# Revit family: Base_Cabinets-Teknion-RHBW_Base_Cabinet_with_Drawers-R2018
name_source: partatom
category: Furniture
revit_build: Autodesk Revit 2018 (Build: 20190510_1515(x64)
units: mm (PartAtom-declared; Revit-internal decimal feet)

## family parameters
Always vertical = Yes
Cut with Voids When Loaded = No
OmniClass Number = 23.40.20.00
OmniClass Title = General Furniture and Specialties
Room Calculation Point = No
Shared = Yes
Work Plane-Based = No

## types (8) — shared parameters
Assembly Code = E2020200
Manufacturer = Teknion
Manufacturer Fax = 416.661.4586
Part Number = RHBW
Product Documentation Link = https://www.teknion.com
Product Line = Modular Cabinets
Product Page URL = https://www.teknion.com
Series = Modular Cabinets
Sustainability Data = https://www.teknion.com
URL = www.teknion.com
Unit Weight URL = http://www.teknion.com
Warranty = http://www.teknion.com

## per-type parameters (varying)
| type | Depth | Description | Four Drawers | Height | Model | Three Drawers | Three Drawers Hole Depth |
| Three Drawers, 24" Depth, 33" Height | 24 " | Base Cabinet with Drawers. Three Drawers, 24" Depth, 33" Height | No | 32.5 " | RHBWT24__33 | Yes | 3.201 " |
| Three Drawers, 29" Depth, 33" Height | 29 " | Base Cabinet with Drawers. Three Drawers, 29" Depth, 33" Height | No | 32.5 " | RHBWT29__33 | Yes | 3.201 " |
| Three Drawers, 29" Depth, 35" Height | 29 " | Base Cabinet with Drawers. Three Drawers, 29" Depth, 35" Height | No | 35 " | RHBWT29__35 | Yes | 3.201 " |
| Three Drawers, 24" Depth, 35" Height | 24 " | Base Cabinet with Drawers. Three Drawers, 24" Depth, 35" Height | No | 35 " | RHBWT24__35 | Yes | 3.201 " |
| Four Drawers, 24" Depth, 33" Height | 24 " | Base Cabinet with Drawers. Four Drawers, 24" Depth, 33" Height | Yes | 32.5 " | RHBWF24__33 | No | 0.5 " |
| Four Drawers, 29" Depth, 33" Height | 29 " | Base Cabinet with Drawers. Four Drawers, 29" Depth, 33" Height | Yes | 32.5 " | RHBWF29__33 | No | 0.5 " |
| Four Drawers, 24" Depth, 35" Height | 24 " | Base Cabinet with Drawers. Four Drawers, 24" Depth, 35" Height | Yes | 35 " | RHBWF24__35 | No | 0.5 " |
| Four Drawers, 29" Depth, 35" Height | 29 " | Base Cabinet with Drawers. Four Drawers, 29" Depth, 35" Height | Yes | 35 " | RHBWF29__35 | No | 0.5 " |

## geometry (parser evidence)
native form markers: Sweep x2
no freeform markers — native parametric forms only
